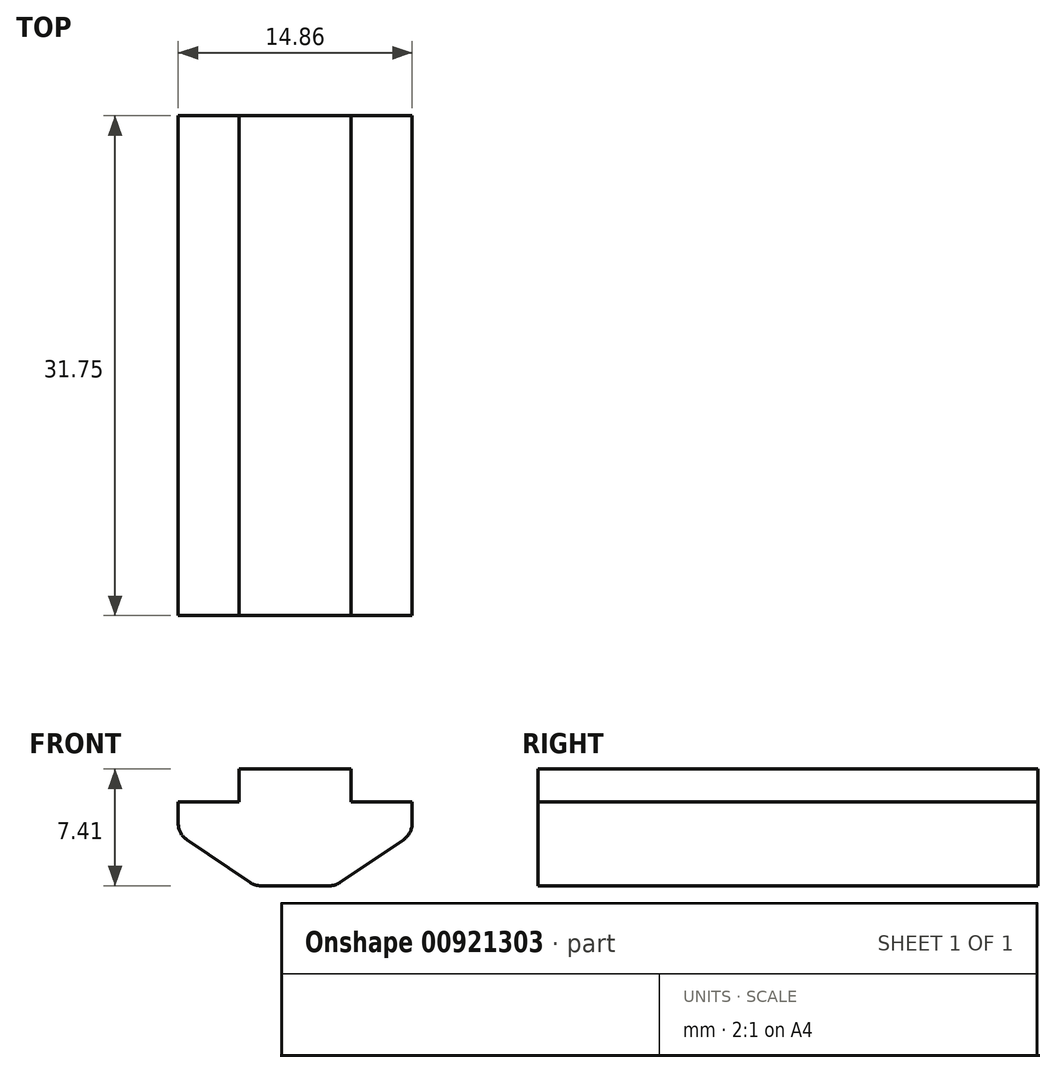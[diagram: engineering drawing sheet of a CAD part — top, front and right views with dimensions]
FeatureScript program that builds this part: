
annotation { "Feature Type Name" : "Feature", "Feature Type Description" : "" }
export const myFeature = defineFeature(function(context is Context, id is Id, definition is map)
    precondition{}
    {
        {
            var Q0;
            Q0=qCreatedBy(makeId("Front.planeOp"),FACE);
            var sketch = newSketch(context, id + "F0", { "sketchPlane" : qUnion([Q0])});
            skLineSegment(sketch, "E0.bottom", {"start": v(-3.56, 2.08) * mm, "end": v(3.56, 2.08) * mm});
            skLineSegment(sketch, "E0.left", {"start": v(-3.56, 2.08) * mm, "end": v(-3.56, 0) * mm});
            skLineSegment(sketch, "E0.right", {"start": v(3.56, 2.08) * mm, "end": v(3.56, 0) * mm});
            skLineSegment(sketch, "E1.bottom", {"start": v(-7.43, 0) * mm, "end": v(-3.56, 0) * mm});
            skLineSegment(sketch, "E1.left", {"start": v(-7.43, 0) * mm, "end": v(-7.43, -2.03) * mm});
            skLineSegment(sketch, "E1.right", {"start": v(7.43, 0) * mm, "end": v(7.43, -2.03) * mm});
            skLineSegment(sketch, "E2.top", {"start": v(-2.54, -5.33) * mm, "end": v(2.54, -5.33) * mm});
            skLineSegment(sketch, "E3.trimOffspring", {"start": v(3.56, 0) * mm, "end": v(7.43, 0) * mm});
            skLineSegment(sketch, "E4", {"start": v(-7.43, -2.03) * mm, "end": v(-2.54, -5.33) * mm});
            skLineSegment(sketch, "E5", {"start": v(7.43, -2.03) * mm, "end": v(2.54, -5.33) * mm});
            skSolve(sketch);
        }
        {
            var Q0;
            Q0=makeQuery(id+"F0.imprint","IMPRINT",FACE,{"disambiguationData":[TD([[makeQuery(id+"F0.imprint","IMPRINT",EDGE,{"derivedFrom":sQuery(id+"F0.wireOp",EDGE,"E0.bottom")}),-1.0]])]});
            var Q1;
            {var subQ0=sQuery(id+"F0.wireOp",EDGE,"E1.left");Q1=makeQuery(id+"F0.imprint","IMPRINT",FACE,{"disambiguationData":[TD([[makeQuery(id+"F0.imprint","IMPRINT",EDGE,{"derivedFrom":subQ0}),1.0]])]});}
            var Q2;
            Q2=makeQuery(id+"F0.imprint","IMPRINT",FACE,{"disambiguationData":[TD([[makeQuery(id+"F0.imprint","IMPRINT",EDGE,{"derivedFrom":sQuery(id+"F0.wireOp",EDGE,"E2.bottom")}),-1.0]])]});
            extrude(context, id + "F1", {"entities" : qUnion([Q0, Q1, Q2]), "depth" : 31.75 * mm, "offsetDistance" : 25.4 * mm});
        }
        {
            var Q0;
            Q0=makeQuery(id+"F1.opExtrude","SWEPT_FACE",FACE,{"disambiguationData":[OSD([sQuery(id+"F0.wireOp",EDGE,"E0.bottom")])]});
            var sketch = newSketch(context, id + "F2", { "sketchPlane" : qUnion([Q0])});
            skCircle(sketch, "E6", {"center": v(0, -21.39) * mm, "radius": 3.38 * mm});
            skCircle(sketch, "E7", {"center": v(0, -7.65) * mm, "radius": 2.54 * mm});
            skPoint(sketch, "E7.centerSnap0", {"position": v(0, 0) * mm});
            skSolve(sketch);
        }
        {
            var Q0;
            Q0=makeQuery(id+"F1.opExtrude","SWEPT_EDGE",EDGE,{"disambiguationData":[OSD([sQuery(id+"F0.wireOp",EDGE,"E1.right"),sQuery(id+"F0.wireOp",EDGE,"E5")])]});
            var Q1;
            Q1=makeQuery(id+"F1.opExtrude","SWEPT_EDGE",EDGE,{"disambiguationData":[OSD([sQuery(id+"F0.wireOp",EDGE,"E2.top"),sQuery(id+"F0.wireOp",EDGE,"E5")])]});
            var Q2;
            Q2=makeQuery(id+"F1.opExtrude","SWEPT_EDGE",EDGE,{"disambiguationData":[OSD([sQuery(id+"F0.wireOp",EDGE,"E2.top"),sQuery(id+"F0.wireOp",EDGE,"E4")])]});
            var Q3;
            Q3=makeQuery(id+"F1.opExtrude","SWEPT_EDGE",EDGE,{"disambiguationData":[OSD([sQuery(id+"F0.wireOp",EDGE,"E1.left"),sQuery(id+"F0.wireOp",EDGE,"E4")])]});
            fillet(context, id + "F3", {"entities" : qUnion([Q0, Q1, Q2, Q3]), "radius" : 1.27 * mm, "tangentPropagation" : true, "allowEdgeOverflow" : false});
        }
    });
